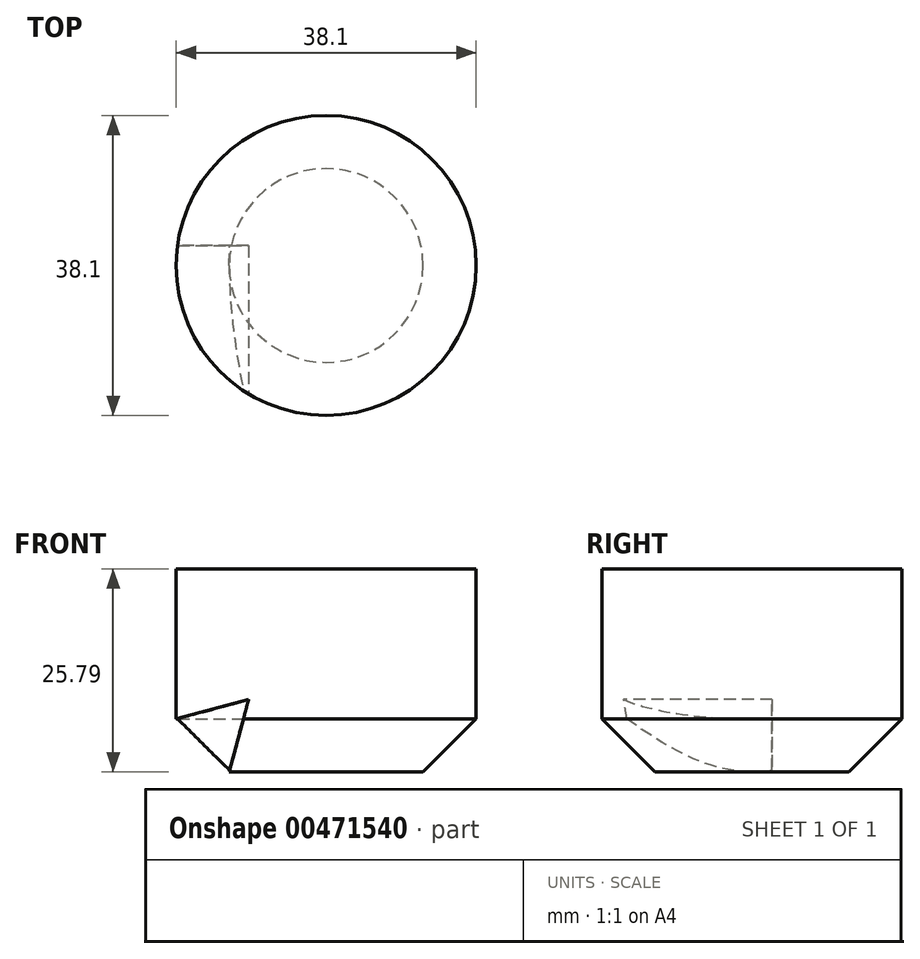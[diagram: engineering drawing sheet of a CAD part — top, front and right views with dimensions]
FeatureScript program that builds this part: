
annotation { "Feature Type Name" : "Feature", "Feature Type Description" : "" }
export const myFeature = defineFeature(function(context is Context, id is Id, definition is map)
    precondition{}
    {
        {
            var Q0;
            Q0=qCreatedBy(makeId("Front.planeOp"),FACE);
            var sketch = newSketch(context, id + "F0", { "sketchPlane" : qUnion([Q0])});
            skLineSegment(sketch, "E0", {"start": v(0, 25.8) * mm, "end": v(-19.05, 25.8) * mm});
            skLineSegment(sketch, "E1", {"start": v(-19.05, 6.74) * mm, "end": v(-12.3, 0) * mm});
            skLineSegment(sketch, "E2", {"start": v(-12.3, 0) * mm, "end": v(0, 0) * mm});
            skLineSegment(sketch, "E3", {"start": v(0, 0) * mm, "end": v(0, 25.8) * mm});
            skLineSegment(sketch, "E4", {"start": v(-19.05, 25.8) * mm, "end": v(-19.05, 6.74) * mm});
            skSolve(sketch);
        }
        {
            var Q0;
            Q0=makeQuery(id+"F0.imprint","IMPRINT",FACE,{"disambiguationData":[TD([[makeQuery(id+"F0.imprint","IMPRINT",EDGE,{"derivedFrom":sQuery(id+"F0.wireOp",EDGE,"E0")}),1.0]])]});
            var Q1;
            Q1=sQuery(id+"F0.wireOp",EDGE,"E3");
            revolve(context, id + "F1", {"entities" : qUnion([Q0]), "axis" : qUnion([Q1]), "revolveType" : RevolveType.FULL});
        }
        {
            var Q0;
            Q0=qCreatedBy(makeId("Front.planeOp"),FACE);
            var sketch = newSketch(context, id + "F2", { "sketchPlane" : qUnion([Q0])});
            skLineSegment(sketch, "E5", {"start": v(-12.3, 0) * mm, "end": v(-9.85, 9.2) * mm});
            skLineSegment(sketch, "E6", {"start": v(-19.05, 6.73) * mm, "end": v(-19.05, 25.8) * mm});
            skLineSegment(sketch, "E7", {"start": v(-9.85, 9.2) * mm, "end": v(-19.05, 6.73) * mm});
            skLineSegment(sketch, "E8", {"start": v(-12.3, 0) * mm, "end": v(-19.05, 6.74) * mm});
            skLineSegment(sketch, "E9", {"start": v(-19.05, 6.73) * mm, "end": v(-12.3, 0) * mm});
            skSolve(sketch);
        }
        {
            var Q0;
            Q0 = qSketchRegion(id + "F2", true);
            extrude(context, id + "F3", {"entities" : qUnion([Q0]), "operationType" : NewBodyOperationType.REMOVE, "oppositeDirection" : true, "depth" : 2.54 * mm});
        }
        {
            var Q0;
            Q0=makeQuery(id+"F3.boolean.opBoolean","COPY",FACE,{"derivedFrom":makeQuery(id+"F3.opExtrude","CAP_FACE",FACE,{"disambiguationData":[OSD([sQuery(id+"F2.wireOp",EDGE,"E5"),sQuery(id+"F2.wireOp",EDGE,"E6"),sQuery(id+"F2.wireOp",EDGE,"E7"),sQuery(id+"F2.wireOp",EDGE,"E8"),sQuery(id+"F2.wireOp",EDGE,"E9")])],"isStart":true})});
            extrude(context, id + "F4", {"entities" : qUnion([Q0]), "operationType" : NewBodyOperationType.REMOVE, "oppositeDirection" : true, "depth" : 25.4 * mm});
        }
    });
